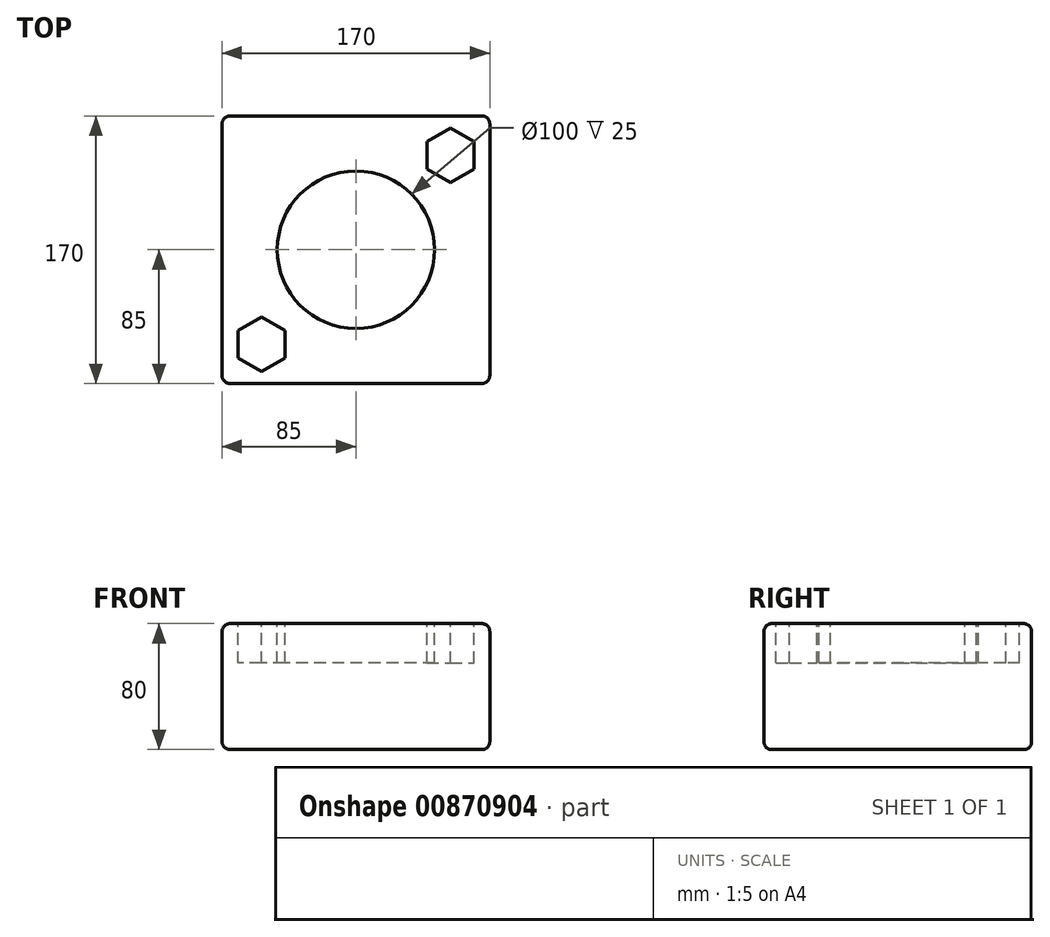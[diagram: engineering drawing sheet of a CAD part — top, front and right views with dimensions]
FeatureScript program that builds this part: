
annotation { "Feature Type Name" : "Feature", "Feature Type Description" : "" }
export const myFeature = defineFeature(function(context is Context, id is Id, definition is map)
    precondition{}
    {
        {
            var Q0;
            Q0=qCreatedBy(makeId("Top.planeOp"),FACE);
            var sketch = newSketch(context, id + "F0", { "sketchPlane" : qUnion([Q0])});
            skLineSegment(sketch, "E0.bottom", {"start": v(-85, 85) * mm, "end": v(85, 85) * mm});
            skLineSegment(sketch, "E0.top", {"start": v(-85, -85) * mm, "end": v(85, -85) * mm});
            skLineSegment(sketch, "E0.left", {"start": v(-85, 85) * mm, "end": v(-85, -85) * mm});
            skLineSegment(sketch, "E0.right", {"start": v(85, 85) * mm, "end": v(85, -85) * mm});
            skPoint(sketch, "E0.middle", {"position": v(0, 0) * mm});
            skSolve(sketch);
        }
        {
            var Q0;
            Q0=makeQuery(id+"F0.imprint","IMPRINT",FACE,{"disambiguationData":[TD([[makeQuery(id+"F0.imprint","IMPRINT",EDGE,{"derivedFrom":sQuery(id+"F0.wireOp",EDGE,"E0.bottom")}),-1.0]])]});
            extrude(context, id + "F1", {"entities" : qUnion([Q0]), "depth" : 80 * mm, "offsetDistance" : 25 * mm});
        }
        {
            var Q0;
            Q0=makeQuery(id+"F1.opExtrude","CAP_FACE",FACE,{"disambiguationData":[OSD([sQuery(id+"F0.wireOp",EDGE,"E0.bottom"),sQuery(id+"F0.wireOp",EDGE,"E0.top"),sQuery(id+"F0.wireOp",EDGE,"E0.left"),sQuery(id+"F0.wireOp",EDGE,"E0.right")])],"isStart":false});
            var sketch = newSketch(context, id + "F2", { "sketchPlane" : qUnion([Q0])});
            skCircle(sketch, "E1", {"center": v(0, 0) * mm, "radius": 50 * mm});
            skCircle(sketch, "E2", {"center": v(0, 0) * mm, "radius": 65 * mm});
            skCircle(sketch, "E3.cCircle", {"center": v(-60, -60) * mm, "radius": 15 * mm, "construction": true});
            skLineSegment(sketch, "E3.0", {"start": v(-75, -68.66) * mm, "end": v(-75, -51.34) * mm});
            skLineSegment(sketch, "E3.1", {"start": v(-75, -51.34) * mm, "end": v(-60, -42.68) * mm});
            skLineSegment(sketch, "E3.2", {"start": v(-60, -42.68) * mm, "end": v(-45, -51.34) * mm});
            skLineSegment(sketch, "E3.3", {"start": v(-45, -51.34) * mm, "end": v(-45, -68.66) * mm});
            skLineSegment(sketch, "E3.4", {"start": v(-45, -68.66) * mm, "end": v(-60, -77.32) * mm});
            skLineSegment(sketch, "E3.5", {"start": v(-60, -77.32) * mm, "end": v(-75, -68.66) * mm});
            skPoint(sketch, "E3.0.midPoint", {"position": v(-75, -60) * mm});
            skCircle(sketch, "E4.cCircle", {"center": v(60, 60) * mm, "radius": 15 * mm, "construction": true});
            skLineSegment(sketch, "E4.0", {"start": v(75, 68.66) * mm, "end": v(75, 51.34) * mm});
            skLineSegment(sketch, "E4.1", {"start": v(75, 51.34) * mm, "end": v(60, 42.68) * mm});
            skLineSegment(sketch, "E4.2", {"start": v(60, 42.68) * mm, "end": v(45, 51.34) * mm});
            skLineSegment(sketch, "E4.3", {"start": v(45, 51.34) * mm, "end": v(45, 68.66) * mm});
            skLineSegment(sketch, "E4.4", {"start": v(45, 68.66) * mm, "end": v(60, 77.32) * mm});
            skLineSegment(sketch, "E4.5", {"start": v(60, 77.32) * mm, "end": v(75, 68.66) * mm});
            skPoint(sketch, "E4.0.midPoint", {"position": v(75, 60) * mm});
            skSolve(sketch);
        }
        {
            var Q0;
            Q0=makeQuery(id+"F2.imprint","IMPRINT",FACE,{"disambiguationData":[TD([[makeQuery(id+"F2.imprint","IMPRINT",EDGE,{"derivedFrom":sQuery(id+"F2.wireOp",EDGE,"E1")}),1.0]])]});
            var Q1;
            Q1=makeQuery(id+"F2.imprint","IMPRINT",FACE,{"disambiguationData":[TD([[makeQuery(id+"F2.imprint","IMPRINT",EDGE,{"derivedFrom":sQuery(id+"F2.wireOp",EDGE,"E3.0")}),-1.0]])]});
            var Q2;
            Q2=makeQuery(id+"F2.imprint","IMPRINT",FACE,{"disambiguationData":[TD([[makeQuery(id+"F2.imprint","IMPRINT",EDGE,{"derivedFrom":sQuery(id+"F2.wireOp",EDGE,"E4.0")}),-1.0]])]});
            extrude(context, id + "F3", {"entities" : qUnion([Q0, Q1, Q2]), "operationType" : NewBodyOperationType.REMOVE, "oppositeDirection" : true, "depth" : 25 * mm, "offsetDistance" : 25 * mm});
        }
        {
            var Q0;
            Q0=makeQuery(id+"F1.opExtrude","SWEPT_EDGE",EDGE,{"disambiguationData":[OSD([sQuery(id+"F0.wireOp",EDGE,"E0.top"),sQuery(id+"F0.wireOp",EDGE,"E0.right")])]});
            var Q1;
            Q1=makeQuery(id+"F1.opExtrude","SWEPT_EDGE",EDGE,{"disambiguationData":[OSD([sQuery(id+"F0.wireOp",EDGE,"E0.bottom"),sQuery(id+"F0.wireOp",EDGE,"E0.right")])]});
            var Q2;
            Q2=makeQuery(id+"F1.opExtrude","SWEPT_EDGE",EDGE,{"disambiguationData":[OSD([sQuery(id+"F0.wireOp",EDGE,"E0.bottom"),sQuery(id+"F0.wireOp",EDGE,"E0.left")])]});
            var Q3;
            Q3=makeQuery(id+"F1.opExtrude","SWEPT_EDGE",EDGE,{"disambiguationData":[OSD([sQuery(id+"F0.wireOp",EDGE,"E0.top"),sQuery(id+"F0.wireOp",EDGE,"E0.left")])]});
            fillet(context, id + "F4", {"entities" : qUnion([Q0, Q1, Q2, Q3]), "radius" : 5 * mm, "tangentPropagation" : true, "allowEdgeOverflow" : false});
        }
        {
            var Q0;
            Q0=makeQuery(id+"F1.opExtrude","CAP_EDGE",EDGE,{"disambiguationData":[OSD([sQuery(id+"F0.wireOp",EDGE,"E0.left")])],"isStart":false});
            var Q1;
            Q1=makeQuery(id+"F1.opExtrude","CAP_EDGE",EDGE,{"disambiguationData":[OSD([sQuery(id+"F0.wireOp",EDGE,"E0.right")])],"isStart":true});
            fillet(context, id + "F5", {"entities" : qUnion([Q0, Q1]), "radius" : 5 * mm, "tangentPropagation" : true, "allowEdgeOverflow" : false});
        }
    });
